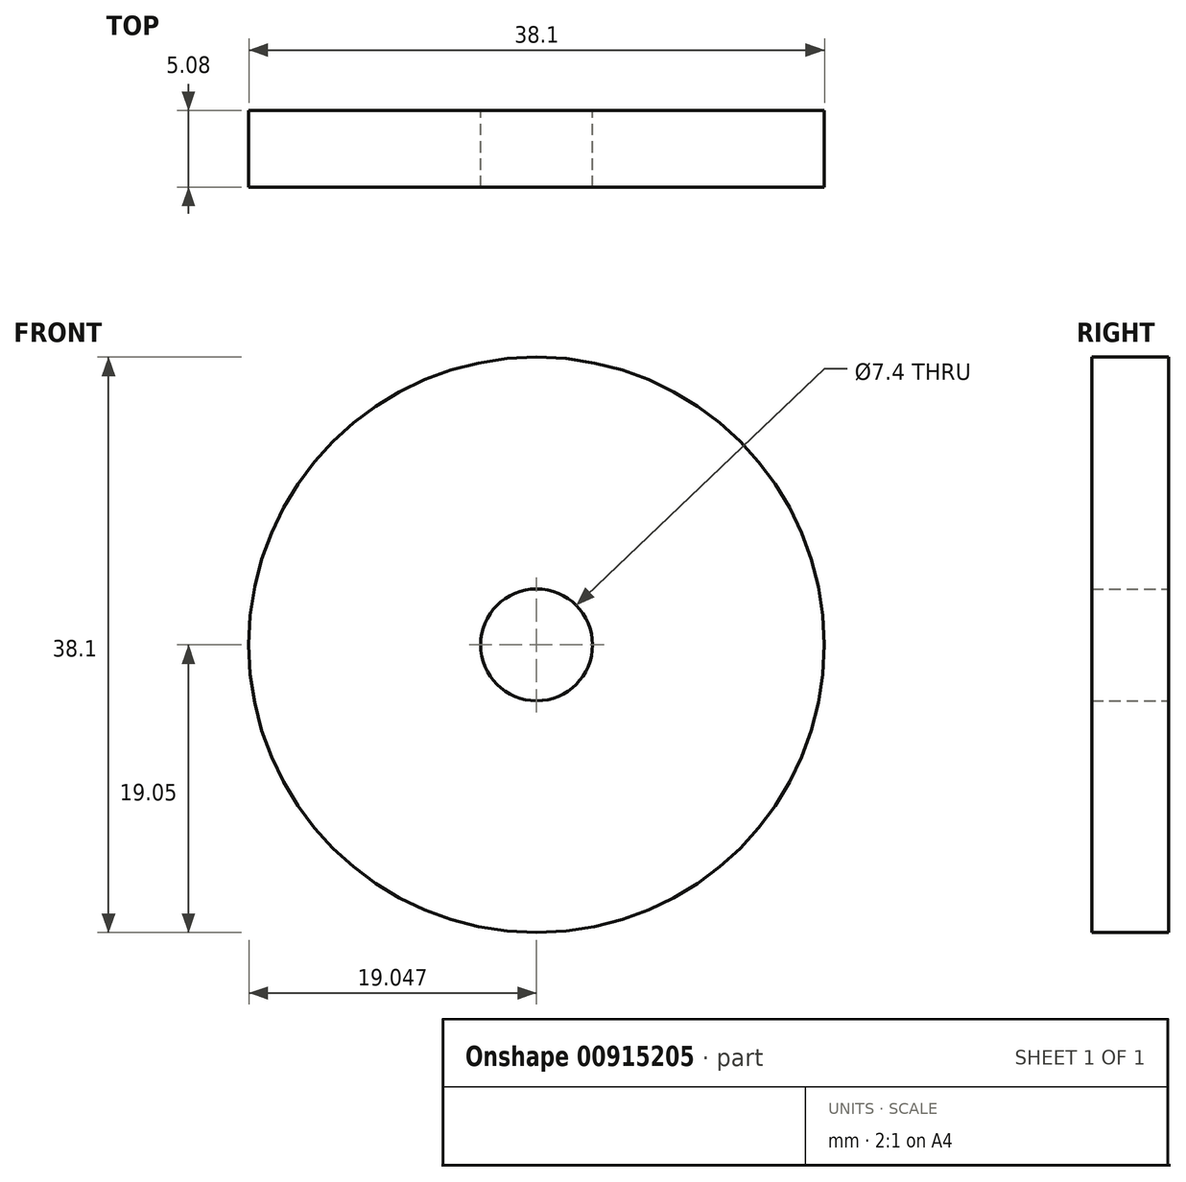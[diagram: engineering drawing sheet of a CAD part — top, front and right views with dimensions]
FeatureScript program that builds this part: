
annotation { "Feature Type Name" : "Feature", "Feature Type Description" : "" }
export const myFeature = defineFeature(function(context is Context, id is Id, definition is map)
    precondition{}
    {
        {
            var Q0;
            Q0=qCreatedBy(makeId("Front.planeOp"),FACE);
            var sketch = newSketch(context, id + "F0", { "sketchPlane" : qUnion([Q0])});
            skCircle(sketch, "E0", {"center": v(1.79, 0) * mm, "radius": 19.05 * mm});
            skCircle(sketch, "E1", {"center": v(1.79, 0) * mm, "radius": 3.7 * mm});
            skSolve(sketch);
        }
        {
            var Q0;
            Q0 = qSketchRegion(id + "F0", true);
            extrude(context, id + "F1", {"entities" : qUnion([Q0]), "depth" : 5.08 * mm, "offsetDistance" : 25.4 * mm});
        }
    });
